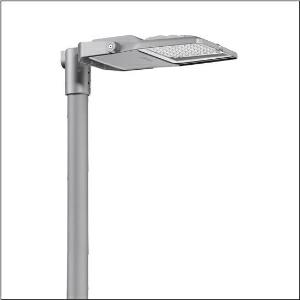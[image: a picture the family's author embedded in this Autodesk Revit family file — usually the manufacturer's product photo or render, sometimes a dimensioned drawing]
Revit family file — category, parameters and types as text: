
# Revit family: floodlight_fl_21_mini___pl43_5xa7775b2a3a_f7a6
name_source: partatom
category: Lighting Fixtures
units: mm (PartAtom-declared; Revit-internal decimal feet)

## family parameters
Cut with Voids When Loaded = No
Host = Face
Light Source = No
Part Type = Normal
Room Calculation Point = No
Round Connector Dimension = Use Diameter
Shared = No

## types (1)
- --- (1 x LED, 6390 lm, 45.7 W, 3000K)
    Apparent Load = 46 VA
    CIE Flux Codes = 27 78 99 100 100
    Color Rendering = 70
    Color Temperature = 3000K
    Default Elevation = 1800 mm
    Description = Floodlight FL 21 mini, floodlight, primary light control with lens, of PMMA, primary optical cover: protective disc, of toughened safety glass, transparent, light distribution: PL43, light emission: direct distribution, installation type: surface-mounted, LED, High Power LED, rated luminous flux: 6.390lm, luminous efficacy: 140lm/W, light colour: 730, colour temperature: 3000K, control gear: Smart Interface (Zhaga), control: flexible luminous flux parameterisation, time-dependent luminous flux control, constant luminous flux control, overheat protection, pre-setting: logarithmic dimming characteristic, with terminal, 6-pole, mains connection: 220..240V, AC, 50/60Hz, start of lifetime: 46W, end of service life: 48W, reduction: 22W, luminaire housing, of diecast aluminium, powder-coated, SITECO metallic grey (DB 702S), corrosivity category C5 mid according to DIN EN ISO 12944, suitable for swimming pools, chlorine-resistant, sealing non-destructively replaceable, please order mast flange separately, mast bracket, of steel, galvanised, powder-coated, SITECO metallic grey (DB 702S), Smart Interface above, protection rating (complete): IP66, insulation class (complete): insulation class II (safety insulation), certification: CE, ENEC, VDE, protection symbol: D, impact resistance: IK08, permissible operating ambient temperature: -40..+40°C, permissible operating ambient temperature for outdoor applications: -40..+50°C, standard: DIN EN 12944, LABS conformity tested according to VDMA 24364:2018-05, packaging unit: 1 piece

Light Distribution: PL43
    Height = 70 mm
    Lamp = 1 x LED
    Lamp Light Flux = 6390 lm
    Lamp Power = 45.7 W
    Lamp count = 1
    Length = 485 mm
    Luminous efficacy = 140 lm/W
    Manufacturer = Siteco
    ModVariant = No
    Model = 5XA7775B2A3A
    Mounting Place = Pole
    Mounting Type = Pole annexe
    Number of Poles = 1
    OnlyDefault = Yes
    Power Factor = 1
    Product Name = Floodlight FL 21 mini | PL43
    Product group = floodlight | pylon annexe
    ProductGroupID = 6201
    Protection Class = Protection class II
    Protection Degree = IP 66
    RLX_Detail_Level = 1
    RLX_Emergency_Light_Flux = 0 lm
    RLX_Emergency_Type = 0
    RLX_Emergency_Type_DB = No
    RlxData = <blob elided: 100813 chars, md5=66c50495>
    Socket = socket
    Standby Power = 0 W
    System Light Flux = 6390 lm
    System Power = 46 W
    Type Comments = factory setting: luminous flux: 100 % | dim-lin: 254 | 463 mA
    Type Image = l_1007125.jpg
    URL = http://relux.com
    VarID = @adj_162275
    Voltage = 0 V
    Weight = 0.00 kg
    Width = 337 mm

## geometry (parser evidence)
native form markers: Blend x4, Sweep x12
no freeform markers — native parametric forms only
